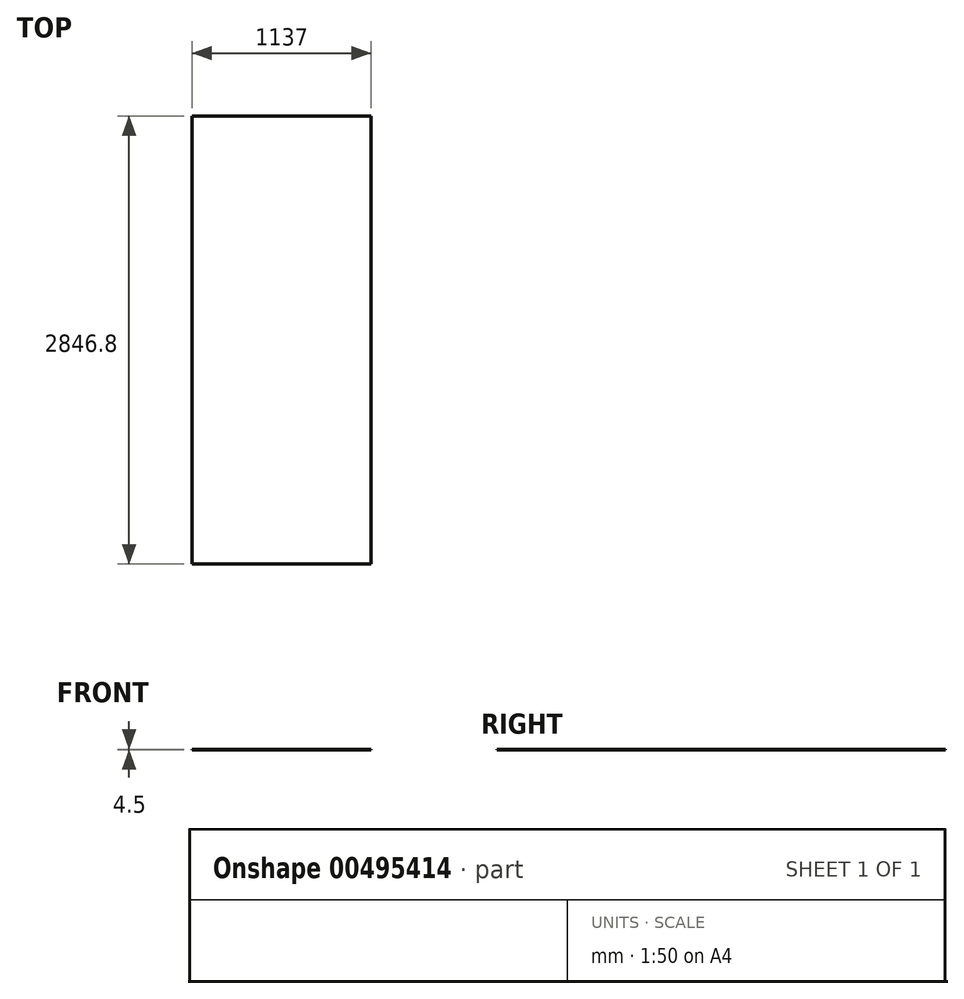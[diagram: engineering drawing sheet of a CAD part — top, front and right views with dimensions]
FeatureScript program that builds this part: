
annotation { "Feature Type Name" : "Feature", "Feature Type Description" : "" }
export const myFeature = defineFeature(function(context is Context, id is Id, definition is map)
    precondition{}
    {
        {
            var Q0;
            Q0=qCreatedBy(makeId("Top.planeOp"),FACE);
            var sketch = newSketch(context, id + "F0", { "sketchPlane" : qUnion([Q0])});
            skLineSegment(sketch, "E0.bottom", {"start": v(0, 0) * mm, "end": v(1137, 0) * mm});
            skLineSegment(sketch, "E0.top", {"start": v(0, 2846.8) * mm, "end": v(1137, 2846.8) * mm});
            skLineSegment(sketch, "E0.left", {"start": v(0, 0) * mm, "end": v(0, 2846.8) * mm});
            skLineSegment(sketch, "E0.right", {"start": v(1137, 0) * mm, "end": v(1137, 2846.8) * mm});
            skSolve(sketch);
        }
        {
            var Q0;
            Q0=makeQuery(id+"F0.imprint","IMPRINT",FACE,{"disambiguationData":[TD([[makeQuery(id+"F0.imprint","IMPRINT",EDGE,{"derivedFrom":sQuery(id+"F0.wireOp",EDGE,"E0.bottom")}),1.0]])]});
            extrude(context, id + "F1", {"entities" : qUnion([Q0]), "depth" : 4.5 * mm});
        }
    });
